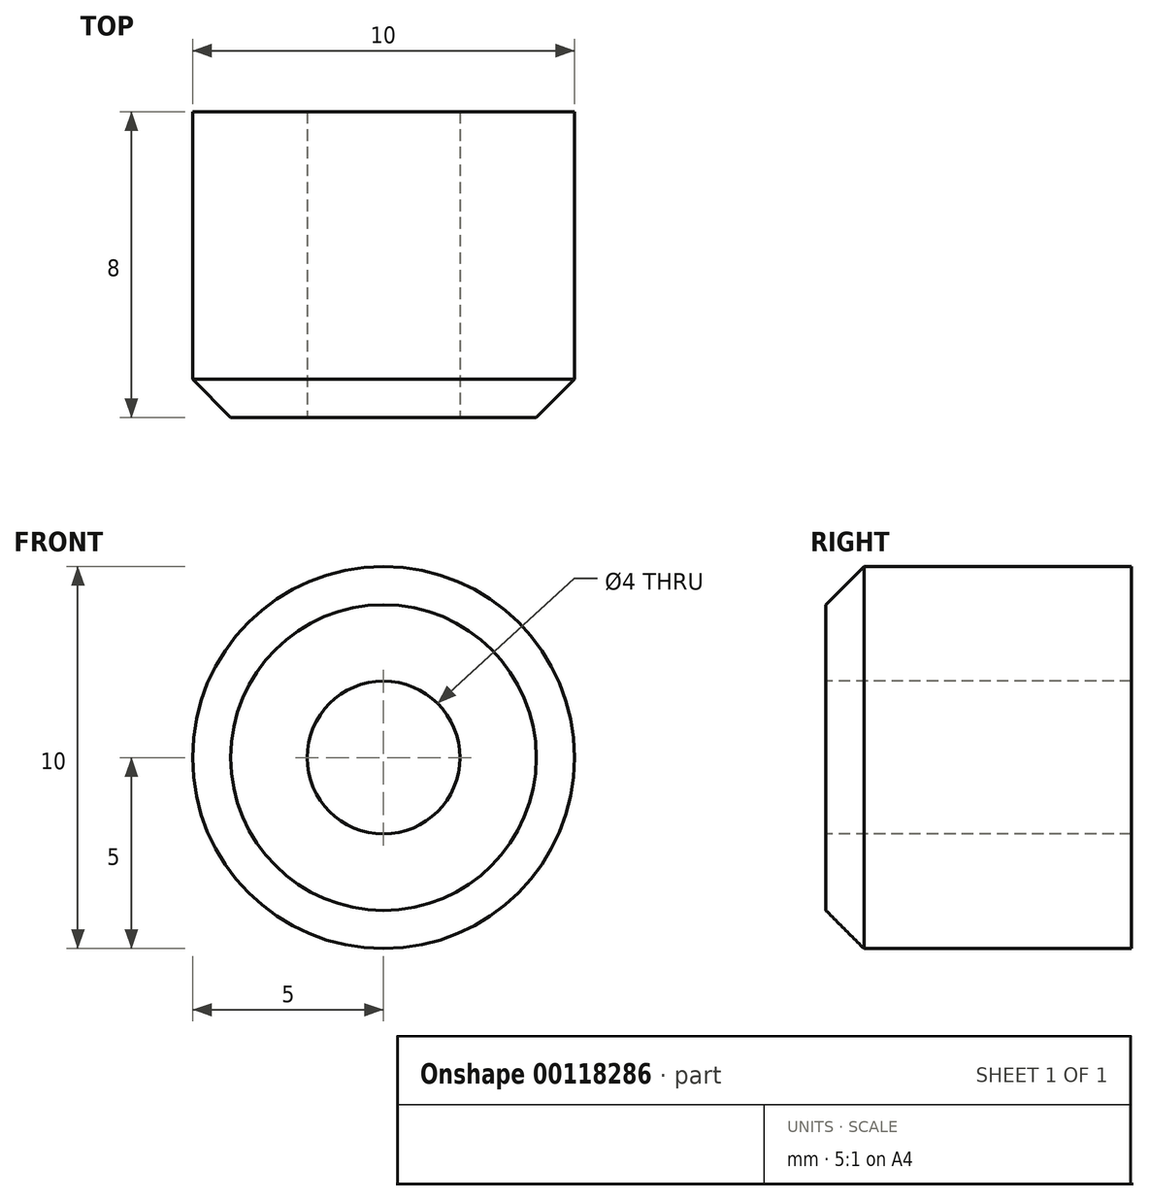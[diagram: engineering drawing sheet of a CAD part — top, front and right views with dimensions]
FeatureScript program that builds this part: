
annotation { "Feature Type Name" : "Feature", "Feature Type Description" : "" }
export const myFeature = defineFeature(function(context is Context, id is Id, definition is map)
    precondition{}
    {
        {
            var Q0;
            Q0=qCreatedBy(makeId("Front.planeOp"),FACE);
            var sketch = newSketch(context, id + "F0", { "sketchPlane" : qUnion([Q0])});
            skCircle(sketch, "E0", {"center": v(0, 0) * mm, "radius": 5 * mm});
            skSolve(sketch);
        }
        {
            var Q0;
            Q0=makeQuery(id+"F0.imprint","IMPRINT",FACE,{"disambiguationData":[TD([[makeQuery(id+"F0.imprint","IMPRINT",EDGE,{"derivedFrom":sQuery(id+"F0.wireOp",EDGE,"E0")}),1.0]])]});
            extrude(context, id + "F1", {"entities" : qUnion([Q0]), "depth" : 8 * mm});
        }
        {
            var Q0;
            Q0=makeQuery(id+"F1.opExtrude","CAP_FACE",FACE,{"disambiguationData":[OSD([sQuery(id+"F0.wireOp",EDGE,"E0")])],"isStart":false});
            var sketch = newSketch(context, id + "F2", { "sketchPlane" : qUnion([Q0])});
            skLineSegment(sketch, "E1", {"start": v(0, 5) * mm, "end": v(0, 0) * mm});
            skSolve(sketch);
        }
        {
            var Q0;
            Q0=sQuery(id+"F2.wireOp",VERTEX,"E1.end");
            var Q1;
            Q1=makeQuery(id+"F1.opExtrude","SWEPT_BODY",BODY,{"disambiguationData":[OSD([sQuery(id+"F0.wireOp",EDGE,"E0")])]});
            hole(context, id + "F3", {"style" : HoleStyle.SIMPLE, "endStyle" : HoleEndStyle.THROUGH, "holeDiameter" : 4 * mm, "locations" : qUnion([Q0]), "scope" : qUnion([Q1]), "isTappedThrough" : true});
        }
        {
            var Q0;
            Q0=makeQuery(id+"F1.opExtrude","CAP_EDGE",EDGE,{"disambiguationData":[OSD([sQuery(id+"F0.wireOp",EDGE,"E0")])],"isStart":false});
            chamfer(context, id + "F4", {"entities" : qUnion([Q0]), "width" : 1 * mm, "tangentPropagation" : true});
        }
    });
